# Revit family: Indoor_Table Lamp_Santa&Cole_Cestita Alubat
name_source: partatom
category: Luminarias
revit_build: Autodesk Revit 2018 (Build: 20170223_1515(x64)
units: mm (PartAtom-declared; Revit-internal decimal feet)

## family parameters
Compartido = No
Corte con vacíos al cargar = No
Cota de conector redondo = Diámetro de uso
Número OmniClass = 23.80.70.00
Origen de luz = Sí
Punto de cálculo de habitación = No
Se basa en plano de trabajo = No
Siempre vertical = Sí
Tipo de pieza = Normal
Título OmniClass = Lighting

## types (2) — shared parameters
Assembly instructions = https://www.santacole.com
Cambio de temperatura de color de luz atenuada = <Ninguno>
Carga aparente = 3 VA
Energy Label = https://www.santacole.com
Fabricante = Santa & Cole
Filtro de color = 16777215
Lampshade Material = Santa&Cole - White Opal Polyehtylene
Load = 3 W
Manufacturer website = http://www.santacole.com
Modelo = Cestita Alubat
Tamaño de símbolo de origen de luz = 610 mm
Technical Information = https://www.santacole.com
URL = https://www.santacole.com

## per-type parameters (varying)
| type | Code | Material Structure |
| Olive Green | CESTF02 | Santa & Cole - Olive Green Aluminium |
| Black | CESTF01 | Santa & Cole - Black Matte Aluminium |
